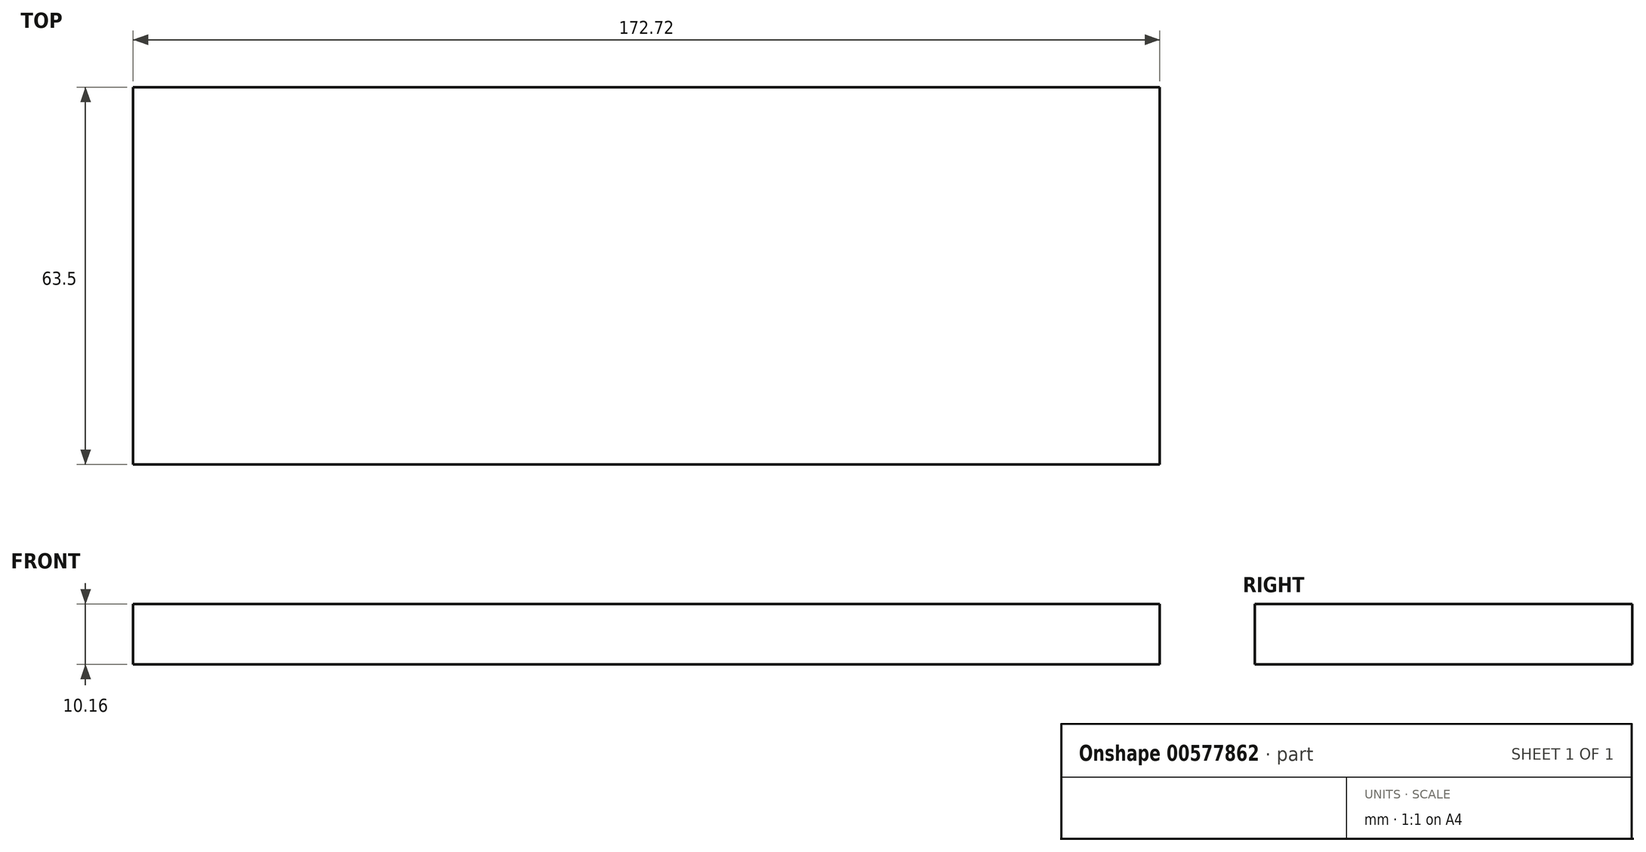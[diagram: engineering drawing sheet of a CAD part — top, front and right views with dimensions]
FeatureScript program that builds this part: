
annotation { "Feature Type Name" : "Feature", "Feature Type Description" : "" }
export const myFeature = defineFeature(function(context is Context, id is Id, definition is map)
    precondition{}
    {
        {
            var Q0;
            Q0=qCreatedBy(makeId("Front.planeOp"),FACE);
            var sketch = newSketch(context, id + "F0", { "sketchPlane" : qUnion([Q0])});
            skLineSegment(sketch, "E0.bottom", {"start": v(-86.36, 5.08) * mm, "end": v(86.36, 5.08) * mm});
            skLineSegment(sketch, "E0.top", {"start": v(-86.36, -5.08) * mm, "end": v(86.36, -5.08) * mm});
            skLineSegment(sketch, "E0.left", {"start": v(-86.36, 5.08) * mm, "end": v(-86.36, -5.08) * mm});
            skLineSegment(sketch, "E0.right", {"start": v(86.36, 5.08) * mm, "end": v(86.36, -5.08) * mm});
            skPoint(sketch, "E0.middle", {"position": v(0, 0) * mm});
            skLineSegment(sketch, "E1.bottom", {"start": v(-86.36, 5.08) * mm, "end": v(-76.2, 5.08) * mm});
            skLineSegment(sketch, "E1.top", {"start": v(-86.36, 81.28) * mm, "end": v(-76.2, 81.28) * mm});
            skLineSegment(sketch, "E1.left", {"start": v(-86.36, 5.08) * mm, "end": v(-86.36, 81.28) * mm});
            skLineSegment(sketch, "E1.right", {"start": v(-76.2, 5.08) * mm, "end": v(-76.2, 81.28) * mm});
            skLineSegment(sketch, "E2.bottom", {"start": v(86.36, 5.08) * mm, "end": v(76.2, 5.08) * mm});
            skLineSegment(sketch, "E2.top", {"start": v(86.36, 81.28) * mm, "end": v(76.2, 81.28) * mm});
            skLineSegment(sketch, "E2.left", {"start": v(86.36, 5.08) * mm, "end": v(86.36, 81.28) * mm});
            skLineSegment(sketch, "E2.right", {"start": v(76.2, 5.08) * mm, "end": v(76.2, 81.28) * mm});
            skSolve(sketch);
        }
        {
            var Q0;
            Q0=makeQuery(id+"F0.imprint","IMPRINT",FACE,{"disambiguationData":[TD([[makeQuery(id+"F0.imprint","IMPRINT",EDGE,{"derivedFrom":sQuery(id+"F0.wireOp",EDGE,"E1.bottom")}),1.0]])]});
            var Q1;
            Q1=makeQuery(id+"F0.imprint","IMPRINT",FACE,{"disambiguationData":[TD([[makeQuery(id+"F0.imprint","IMPRINT",EDGE,{"derivedFrom":sQuery(id+"F0.wireOp",EDGE,"E2.bottom")}),-1.0]])]});
            var Q2;
            Q2=makeQuery(id+"F0.imprint","IMPRINT",FACE,{"disambiguationData":[TD([[makeQuery(id+"F0.imprint","IMPRINT",EDGE,{"derivedFrom":sQuery(id+"F0.wireOp",EDGE,"E0.bottom")}),-1.0]])]});
            extrude(context, id + "F1", {"entities" : qUnion([Q0, Q1, Q2]), "endBound" : BoundingType.SYMMETRIC, "depth" : 63.5 * mm, "offsetDistance" : 25.4 * mm});
        }
        {
            var Q0;
            Q0=makeQuery(id+"F1.opExtrude","SWEPT_FACE",FACE,{"disambiguationData":[OSD([sQuery(id+"F0.wireOp",EDGE,"E0.right"),sQuery(id+"F0.wireOp",EDGE,"E2.left")])]});
            var sketch = newSketch(context, id + "F2", { "sketchPlane" : qUnion([Q0])});
            skCircle(sketch, "E3", {"center": v(11.43, 35.56) * mm, "radius": 7.62 * mm});
            skSolve(sketch);
        }
        {
            var Q0;
            Q0=sQuery(id+"F2.wireOp",VERTEX,"E3.center");
            var Q1;
            Q1=makeQuery(id+"F1.opExtrude","SWEPT_BODY",BODY,{"disambiguationData":[OSD([sQuery(id+"F0.wireOp",EDGE,"E0.bottom"),sQuery(id+"F0.wireOp",EDGE,"E0.top"),sQuery(id+"F0.wireOp",EDGE,"E0.left"),sQuery(id+"F0.wireOp",EDGE,"E0.right"),sQuery(id+"F0.wireOp",EDGE,"E1.top"),sQuery(id+"F0.wireOp",EDGE,"E1.left"),sQuery(id+"F0.wireOp",EDGE,"E1.right"),sQuery(id+"F0.wireOp",EDGE,"E2.top"),sQuery(id+"F0.wireOp",EDGE,"E2.left"),sQuery(id+"F0.wireOp",EDGE,"E2.right")])]});
            hole(context, id + "F3", {"style" : HoleStyle.SIMPLE, "endStyle" : HoleEndStyle.BLIND, "holeDiameter" : 17.78 * mm, "holeDepth" : 12.7 * mm, "isTappedThrough" : true, "tappedDepth" : 12.7 * mm, "tapClearance" : 3, "locations" : qUnion([Q0]), "scope" : qUnion([Q1])});
        }
        {
            var Q0;
            Q0=makeQuery(id+"F1.opExtrude","SWEPT_FACE",FACE,{"disambiguationData":[OSD([sQuery(id+"F0.wireOp",EDGE,"E0.left"),sQuery(id+"F0.wireOp",EDGE,"E1.left")])]});
            var sketch = newSketch(context, id + "F4", { "sketchPlane" : qUnion([Q0])});
            skCircle(sketch, "E4", {"center": v(11.43, 60.96) * mm, "radius": 7.62 * mm});
            skSolve(sketch);
        }
        {
            var Q0;
            Q0=sQuery(id+"F4.wireOp",VERTEX,"E4.center");
            var Q1;
            Q1=makeQuery(id+"F1.opExtrude","SWEPT_BODY",BODY,{"disambiguationData":[OSD([sQuery(id+"F0.wireOp",EDGE,"E0.bottom"),sQuery(id+"F0.wireOp",EDGE,"E0.top"),sQuery(id+"F0.wireOp",EDGE,"E0.left"),sQuery(id+"F0.wireOp",EDGE,"E0.right"),sQuery(id+"F0.wireOp",EDGE,"E1.top"),sQuery(id+"F0.wireOp",EDGE,"E1.left"),sQuery(id+"F0.wireOp",EDGE,"E1.right"),sQuery(id+"F0.wireOp",EDGE,"E2.top"),sQuery(id+"F0.wireOp",EDGE,"E2.left"),sQuery(id+"F0.wireOp",EDGE,"E2.right")])]});
            hole(context, id + "F5", {"style" : HoleStyle.SIMPLE, "endStyle" : HoleEndStyle.BLIND, "holeDiameter" : 17.78 * mm, "holeDepth" : 12.7 * mm, "isTappedThrough" : true, "tappedDepth" : 12.7 * mm, "tapClearance" : 3, "locations" : qUnion([Q0]), "scope" : qUnion([Q1])});
        }
    });
